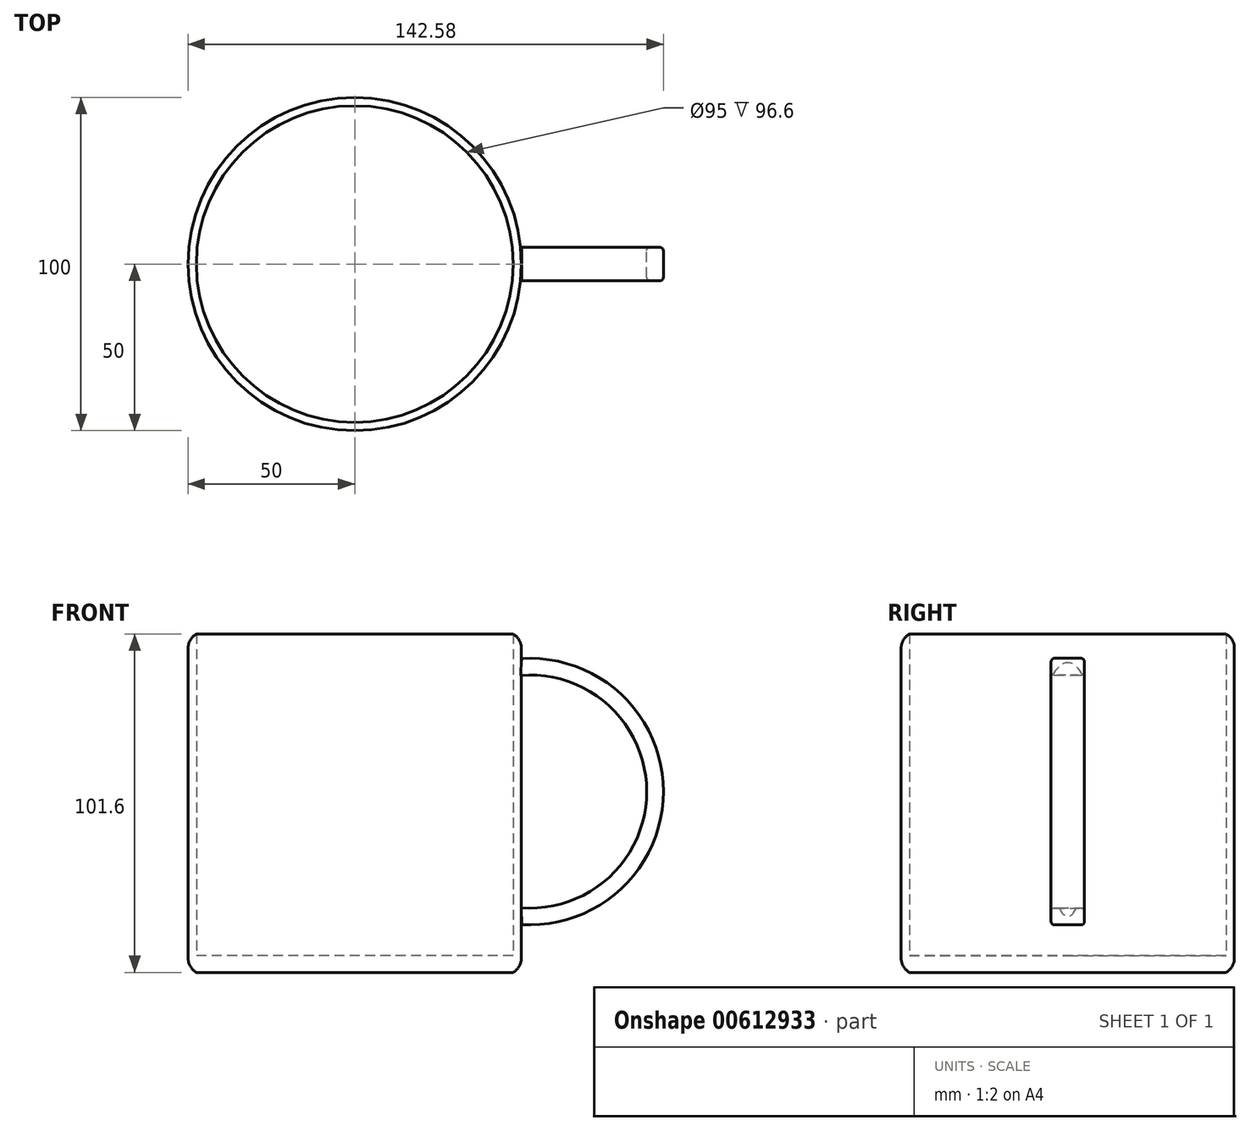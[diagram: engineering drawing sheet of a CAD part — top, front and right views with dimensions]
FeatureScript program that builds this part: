
annotation { "Feature Type Name" : "Feature", "Feature Type Description" : "" }
export const myFeature = defineFeature(function(context is Context, id is Id, definition is map)
    precondition{}
    {
        {
            var Q0;
            Q0=qCreatedBy(makeId("Top.planeOp"),FACE);
            var sketch = newSketch(context, id + "F0", { "sketchPlane" : qUnion([Q0])});
            skCircle(sketch, "E0", {"center": v(0, 0) * mm, "radius": 50 * mm});
            skCircle(sketch, "E1", {"center": v(0, 0) * mm, "radius": 47.5 * mm});
            skSolve(sketch);
        }
        {
            var Q0;
            Q0 = qSketchRegion(id + "F0", true);
            extrude(context, id + "F1", {"entities" : qUnion([Q0]), "depth" : 101.6 * mm, "offsetDistance" : 25.4 * mm});
        }
        {
            var Q0;
            Q0=makeQuery(id+"F1.opExtrude","CAP_EDGE",EDGE,{"disambiguationData":[OSD([sQuery(id+"F0.wireOp",EDGE,"E0")])],"isStart":false});
            fillet(context, id + "F2", {"entities" : qUnion([Q0]), "radius" : 5.08 * mm, "tangentPropagation" : true, "allowEdgeOverflow" : false});
        }
        {
            var Q0;
            Q0=makeQuery(id+"F1.opExtrude","CAP_EDGE",EDGE,{"disambiguationData":[OSD([sQuery(id+"F0.wireOp",EDGE,"E0")])],"isStart":true});
            fillet(context, id + "F3", {"entities" : qUnion([Q0]), "radius" : 5.08 * mm, "tangentPropagation" : true, "allowEdgeOverflow" : false});
        }
        {
            var Q0;
            Q0=makeQuery(id+"F0.imprint","IMPRINT",FACE,{"disambiguationData":[TD([[makeQuery(id+"F0.imprint","IMPRINT",EDGE,{"derivedFrom":sQuery(id+"F0.wireOp",EDGE,"E1")}),1.0]])]});
            extrude(context, id + "F4", {"entities" : qUnion([Q0]), "operationType" : NewBodyOperationType.ADD, "depth" : 5 * mm, "offsetDistance" : 25.4 * mm});
        }
        {
            var Q0;
            Q0=qCreatedBy(makeId("Front.planeOp"),FACE);
            var sketch = newSketch(context, id + "F5", { "sketchPlane" : qUnion([Q0])});
            skArc(sketch, "E2", {"start": v(50.07, 14.35) * mm, "mid": v(92.58, 54.27) * mm, "end": v(50.07, 94.2) * mm});
            skArc(sketch, "E3", {"start": v(49.93, 19.37) * mm, "mid": v(87.58, 54.34) * mm, "end": v(49.79, 89.16) * mm});
            skLineSegment(sketch, "E4", {"start": v(50.07, 94.2) * mm, "end": v(49.79, 89.16) * mm});
            skLineSegment(sketch, "E5", {"start": v(49.93, 19.37) * mm, "end": v(50.07, 14.35) * mm});
            skSolve(sketch);
        }
        {
            var Q0;
            Q0 = qSketchRegion(id + "F5", true);
            extrude(context, id + "F6", {"entities" : qUnion([Q0]), "operationType" : NewBodyOperationType.ADD, "endBound" : BoundingType.SYMMETRIC, "depth" : 10 * mm, "offsetDistance" : 25.4 * mm});
        }
        {
            var Q0;
            Q0=makeQuery(id+"F6.opExtrude","CAP_EDGE",EDGE,{"disambiguationData":[OSD([sQuery(id+"F5.wireOp",EDGE,"E2")])],"isStart":false});
            var Q1;
            Q1=makeQuery(id+"F6.opExtrude","CAP_EDGE",EDGE,{"disambiguationData":[OSD([sQuery(id+"F5.wireOp",EDGE,"E2")])],"isStart":true});
            var Q2;
            Q2=makeQuery(id+"F6.opExtrude","CAP_EDGE",EDGE,{"disambiguationData":[OSD([sQuery(id+"F5.wireOp",EDGE,"E3")])],"isStart":true});
            var Q3;
            Q3=makeQuery(id+"F6.opExtrude","CAP_EDGE",EDGE,{"disambiguationData":[OSD([sQuery(id+"F5.wireOp",EDGE,"E3")])],"isStart":false});
            fillet(context, id + "F7", {"entities" : qUnion([Q0, Q1, Q2, Q3]), "radius" : 1 * mm, "tangentPropagation" : true, "allowEdgeOverflow" : false});
        }
    });
